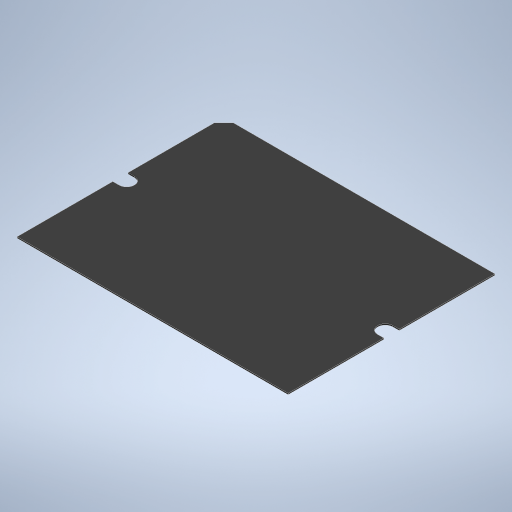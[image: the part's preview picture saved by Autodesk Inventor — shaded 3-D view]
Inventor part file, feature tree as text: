
AUTODESK INVENTOR PART (.ipt)
format: ipt  version: 2023 (Build 270158000, 158)  size: 236,544 bytes
history: native  units: in
note: dims shown in document units (in); Inventor stores cm internally (conversion verified against a paired STEP export)
features: extrude x2, sketch x2, chamfer x1
ambient origin geometry x8: Origin, YZ Plane, XZ Plane, XY Plane, X Axis, Y Axis, Z Axis, Center Point
bodies: Solid1 (feature_tree)
feature tree (5):
  extrude  "Extrusion1"  Depth=2.2244in
  chamfer  "Chamfer1"  Distance=0.0098in
  extrude  "Extrusion2"  TaperAngle=0.0deg  [1 undecoded]
  sketch  "Sketch1"  dims[d0=1.6969in d1=2.2244in d2=0.0098in d3=0.0in]
  sketch  "Sketch2"  dims[d4=0.0787in d5=0.0787in d6=45.0deg d8=0.0in d9=0.0in d14=0.126in d15=0.0512in d16=0.0512in d17=0.126in d18=0.063in]
note: 1 required parameter value undecoded (feature->parameter linkage not recoverable at this tier; creation-order binding heuristic only, values carry confidence <= 0.55)
